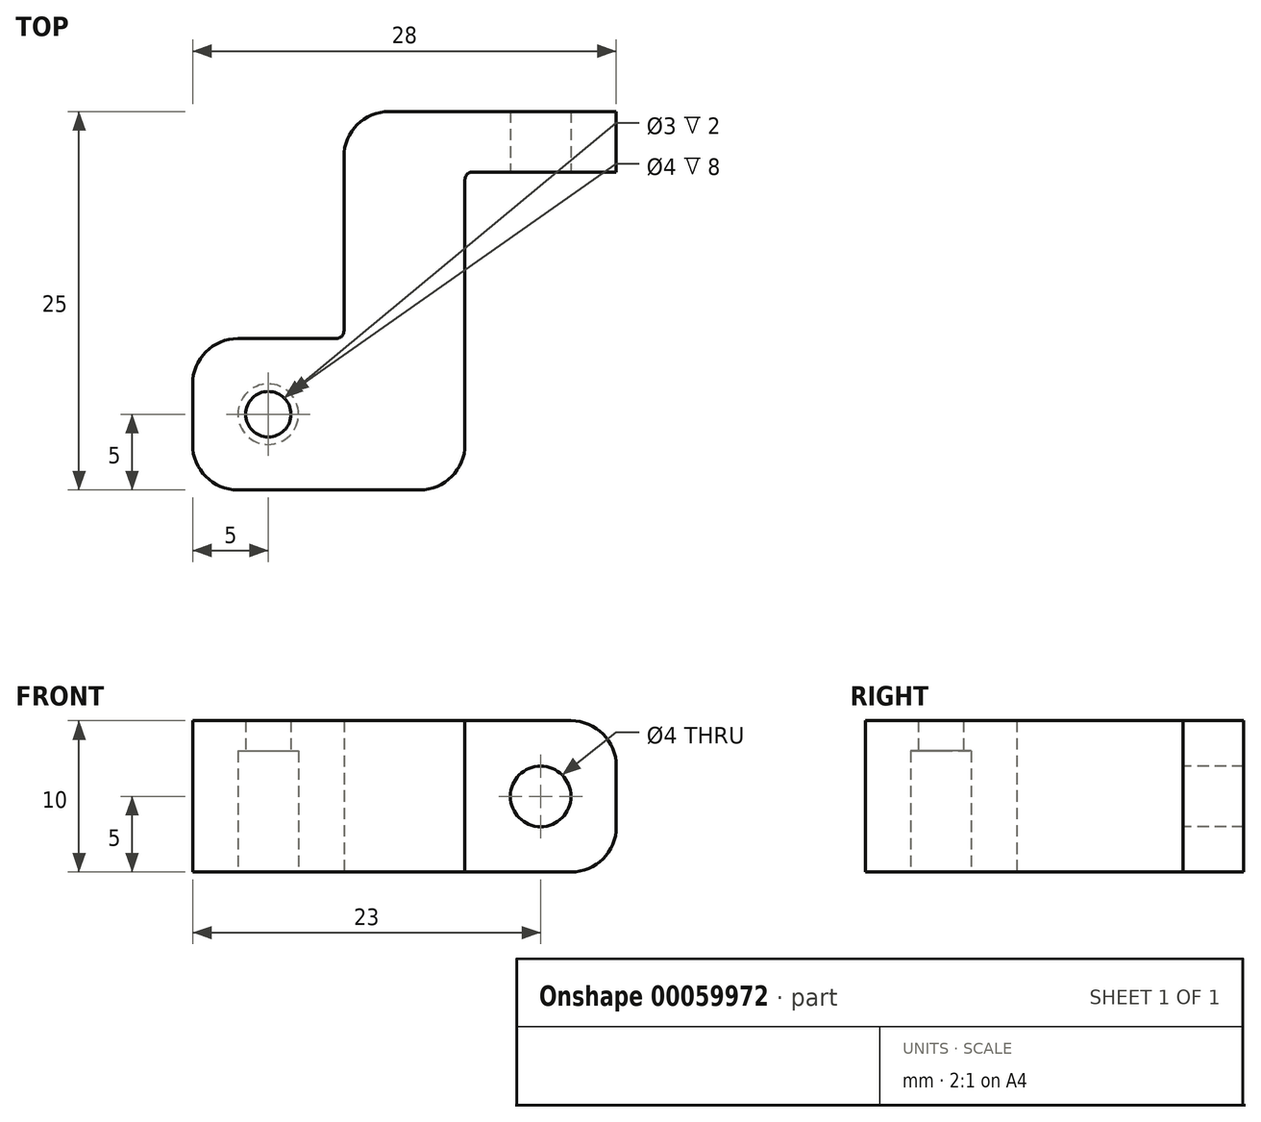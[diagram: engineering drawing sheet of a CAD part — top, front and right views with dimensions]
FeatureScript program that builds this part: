
annotation { "Feature Type Name" : "Feature", "Feature Type Description" : "" }
export const myFeature = defineFeature(function(context is Context, id is Id, definition is map)
    precondition{}
    {
        {
            var Q0;
            Q0=qCreatedBy(makeId("Top.planeOp"),FACE);
            var sketch = newSketch(context, id + "F0", { "sketchPlane" : qUnion([Q0])});
            skLineSegment(sketch, "E0.rect.bottom", {"start": v(4, 12.5) * mm, "end": v(-4, 12.5) * mm});
            skLineSegment(sketch, "E0.rect.top", {"start": v(4, -12.5) * mm, "end": v(-4, -12.5) * mm});
            skLineSegment(sketch, "E0.rect.left", {"start": v(4, 8.5) * mm, "end": v(4, -12.5) * mm});
            skLineSegment(sketch, "E0.rect.right", {"start": v(-4, 12.5) * mm, "end": v(-4, -2.5) * mm});
            skPoint(sketch, "E0.rect.middle", {"position": v(0, 0) * mm});
            skLineSegment(sketch, "E1.bottom", {"start": v(4, 12.5) * mm, "end": v(14, 12.5) * mm});
            skLineSegment(sketch, "E1.top", {"start": v(4, 8.5) * mm, "end": v(14, 8.5) * mm});
            skLineSegment(sketch, "E1.right", {"start": v(14, 12.5) * mm, "end": v(14, 8.5) * mm});
            skLineSegment(sketch, "E2.bottom", {"start": v(-4, -12.5) * mm, "end": v(-14, -12.5) * mm});
            skLineSegment(sketch, "E2.top", {"start": v(-4, -2.5) * mm, "end": v(-14, -2.5) * mm});
            skLineSegment(sketch, "E2.right", {"start": v(-14, -12.5) * mm, "end": v(-14, -2.5) * mm});
            skLineSegment(sketch, "E3", {"start": v(4, 8.5) * mm, "end": v(4, 12.5) * mm, "construction": true});
            skLineSegment(sketch, "E4", {"start": v(-4, -12.5) * mm, "end": v(-4, -2.5) * mm, "construction": true});
            skLineSegment(sketch, "E5", {"start": v(-4, -12.5) * mm, "end": v(-14, -2.5) * mm, "construction": true});
            skSolve(sketch);
        }
        {
            var Q0;
            Q0=qSketchRegion(id+"F0",true);
            extrude(context, id + "F1", {"entities" : qUnion([Q0]), "depth" : 10 * mm});
        }
        {
            var Q0;
            Q0=makeQuery(id+"F1.opExtrude","SWEPT_EDGE",EDGE,{"disambiguationData":[OSD([sQuery(id+"F0.wireOp",EDGE,"E0.rect.bottom"),sQuery(id+"F0.wireOp",EDGE,"E0.rect.right")])]});
            var Q1;
            Q1=makeQuery(id+"F1.opExtrude","SWEPT_EDGE",EDGE,{"disambiguationData":[OSD([sQuery(id+"F0.wireOp",EDGE,"E0.rect.top"),sQuery(id+"F0.wireOp",EDGE,"E0.rect.left")])]});
            fillet(context, id + "F2", {"entities" : qUnion([Q0, Q1]), "radius" : 3 * mm, "tangentPropagation" : true, "allowEdgeOverflow" : false});
        }
        {
            var Q0;
            Q0=makeQuery(id+"F1.opExtrude","CAP_FACE",FACE,{"disambiguationData":[OSD([sQuery(id+"F0.wireOp",EDGE,"E0.rect.bottom"),sQuery(id+"F0.wireOp",EDGE,"E0.rect.top"),sQuery(id+"F0.wireOp",EDGE,"E0.rect.left"),sQuery(id+"F0.wireOp",EDGE,"E0.rect.right"),sQuery(id+"F0.wireOp",EDGE,"E1.bottom"),sQuery(id+"F0.wireOp",EDGE,"E1.top"),sQuery(id+"F0.wireOp",EDGE,"E1.right"),sQuery(id+"F0.wireOp",EDGE,"E2.bottom"),sQuery(id+"F0.wireOp",EDGE,"E2.top"),sQuery(id+"F0.wireOp",EDGE,"E2.right")])],"isStart":true});
            var sketch = newSketch(context, id + "F3", { "sketchPlane" : qUnion([Q0])});
            skLineSegment(sketch, "E6", {"start": v(-4, 2.5) * mm, "end": v(-14, 12.5) * mm, "construction": true});
            skCircle(sketch, "E7", {"center": v(-9, 7.5) * mm, "radius": 1.5 * mm});
            skSolve(sketch);
        }
        {
            var Q0;
            Q0=qSketchRegion(id+"F3",true);
            extrude(context, id + "F4", {"entities" : qUnion([Q0]), "operationType" : NewBodyOperationType.REMOVE, "endBound" : BoundingType.THROUGH_ALL, "oppositeDirection" : true, "depth" : 25 * mm});
        }
        {
            var Q0;
            Q0=makeQuery(id+"F1.opExtrude","CAP_FACE",FACE,{"disambiguationData":[OSD([sQuery(id+"F0.wireOp",EDGE,"E0.rect.bottom"),sQuery(id+"F0.wireOp",EDGE,"E0.rect.top"),sQuery(id+"F0.wireOp",EDGE,"E0.rect.left"),sQuery(id+"F0.wireOp",EDGE,"E0.rect.right"),sQuery(id+"F0.wireOp",EDGE,"E1.bottom"),sQuery(id+"F0.wireOp",EDGE,"E1.top"),sQuery(id+"F0.wireOp",EDGE,"E1.right"),sQuery(id+"F0.wireOp",EDGE,"E2.bottom"),sQuery(id+"F0.wireOp",EDGE,"E2.top"),sQuery(id+"F0.wireOp",EDGE,"E2.right")])],"isStart":true});
            var sketch = newSketch(context, id + "F5", { "sketchPlane" : qUnion([Q0])});
            skCircle(sketch, "E8", {"center": v(-9, 7.5) * mm, "radius": 2 * mm});
            skSolve(sketch);
        }
        {
            var Q0;
            Q0=qSketchRegion(id+"F5",true);
            extrude(context, id + "F6", {"entities" : qUnion([Q0]), "operationType" : NewBodyOperationType.REMOVE, "oppositeDirection" : true, "depth" : 8 * mm});
        }
        {
            var Q0;
            Q0=makeQuery(id+"F1.opExtrude","SWEPT_EDGE",EDGE,{"disambiguationData":[OSD([sQuery(id+"F0.wireOp",EDGE,"E2.top"),sQuery(id+"F0.wireOp",EDGE,"E2.right")])]});
            var Q1;
            Q1=makeQuery(id+"F1.opExtrude","SWEPT_EDGE",EDGE,{"disambiguationData":[OSD([sQuery(id+"F0.wireOp",EDGE,"E2.bottom"),sQuery(id+"F0.wireOp",EDGE,"E2.right")])]});
            fillet(context, id + "F7", {"entities" : qUnion([Q0, Q1]), "radius" : 3 * mm, "tangentPropagation" : true, "allowEdgeOverflow" : false});
        }
        {
            var Q0;
            Q0=makeQuery(id+"F1.opExtrude","SWEPT_FACE",FACE,{"disambiguationData":[OSD([sQuery(id+"F0.wireOp",EDGE,"E1.top")])]});
            var sketch = newSketch(context, id + "F8", { "sketchPlane" : qUnion([Q0])});
            skLineSegment(sketch, "E9", {"start": v(4, 0) * mm, "end": v(14, 10) * mm, "construction": true});
            skCircle(sketch, "E10", {"center": v(9, 5) * mm, "radius": 2 * mm});
            skSolve(sketch);
        }
        {
            var Q0;
            Q0=qSketchRegion(id+"F8",true);
            extrude(context, id + "F9", {"entities" : qUnion([Q0]), "operationType" : NewBodyOperationType.REMOVE, "endBound" : BoundingType.THROUGH_ALL, "oppositeDirection" : true, "depth" : 25 * mm});
        }
        {
            var Q0;
            Q0=makeQuery(id+"F1.opExtrude","CAP_EDGE",EDGE,{"disambiguationData":[OSD([sQuery(id+"F0.wireOp",EDGE,"E1.right")])],"isStart":true});
            var Q1;
            Q1=makeQuery(id+"F1.opExtrude","CAP_EDGE",EDGE,{"disambiguationData":[OSD([sQuery(id+"F0.wireOp",EDGE,"E1.right")])],"isStart":false});
            fillet(context, id + "F10", {"entities" : qUnion([Q0, Q1]), "radius" : 3 * mm, "tangentPropagation" : true, "allowEdgeOverflow" : false});
        }
        {
            var Q0;
            Q0=makeQuery(id+"F1.opExtrude","SWEPT_EDGE",EDGE,{"disambiguationData":[OSD([sQuery(id+"F0.wireOp",EDGE,"E0.rect.left"),sQuery(id+"F0.wireOp",EDGE,"E1.top")])]});
            var Q1;
            Q1=makeQuery(id+"F1.opExtrude","SWEPT_EDGE",EDGE,{"disambiguationData":[OSD([sQuery(id+"F0.wireOp",EDGE,"E0.rect.right"),sQuery(id+"F0.wireOp",EDGE,"E2.top")])]});
            fillet(context, id + "F11", {"entities" : qUnion([Q0, Q1]), "radius" : 0.5 * mm, "tangentPropagation" : true, "allowEdgeOverflow" : false});
        }
    });
